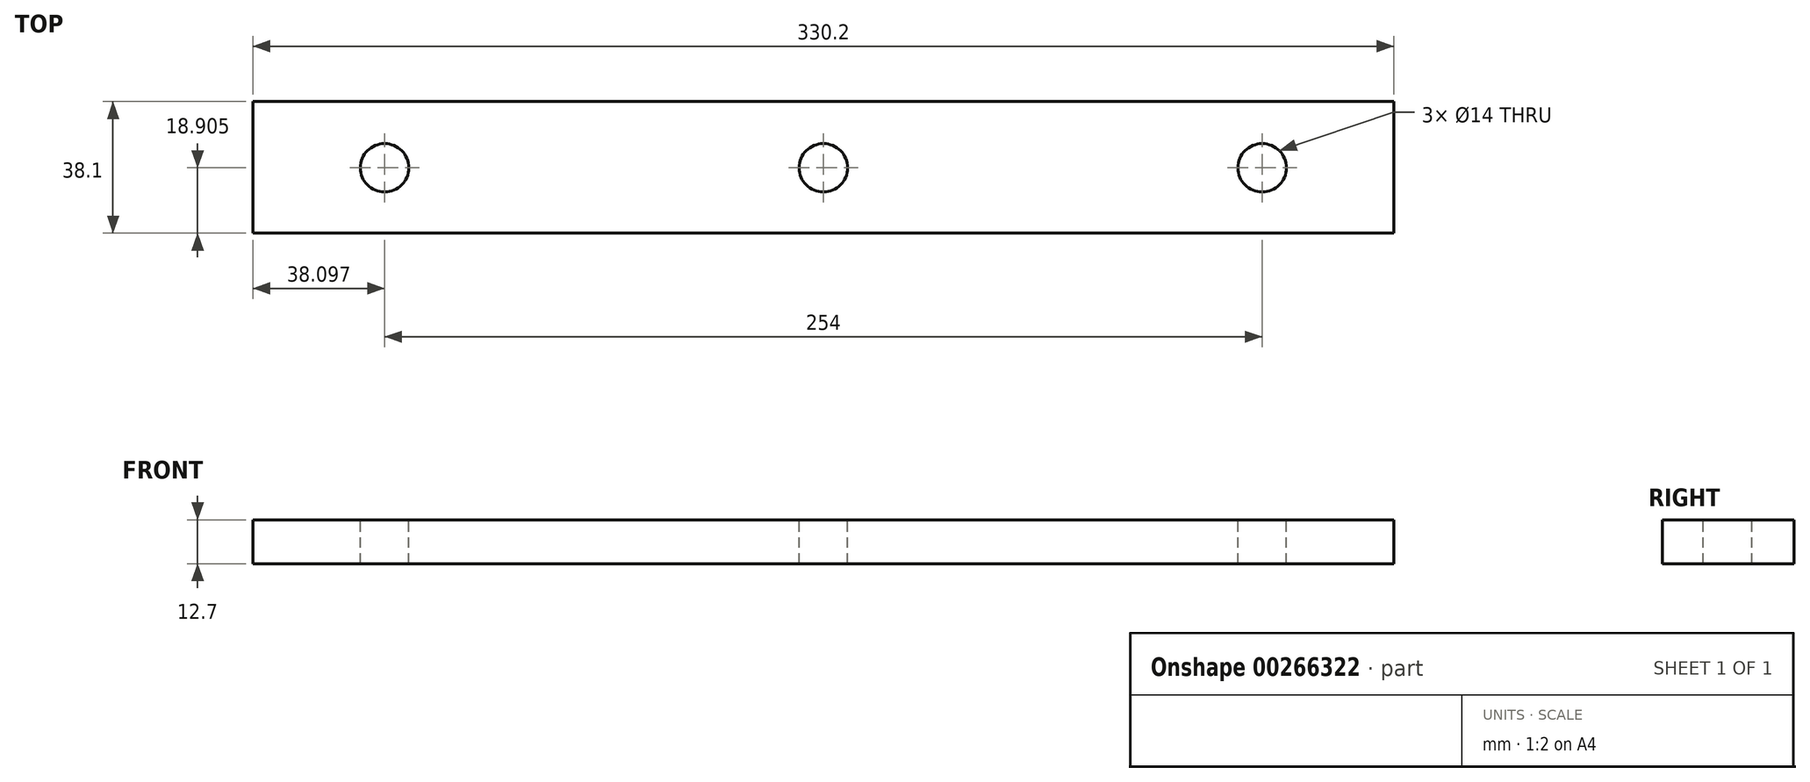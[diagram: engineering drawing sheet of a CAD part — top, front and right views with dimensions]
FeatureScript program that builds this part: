
annotation { "Feature Type Name" : "Feature", "Feature Type Description" : "" }
export const myFeature = defineFeature(function(context is Context, id is Id, definition is map)
    precondition{}
    {
        {
            var Q0;
            Q0=qCreatedBy(makeId("Top.planeOp"),FACE);
            var sketch = newSketch(context, id + "F0", { "sketchPlane" : qUnion([Q0])});
            skLineSegment(sketch, "E0.bottom", {"start": v(-30.27, -15.71) * mm, "end": v(299.93, -15.71) * mm});
            skLineSegment(sketch, "E0.top", {"start": v(-30.27, 22.39) * mm, "end": v(299.93, 22.39) * mm});
            skLineSegment(sketch, "E0.left", {"start": v(-30.27, -15.71) * mm, "end": v(-30.27, 22.39) * mm});
            skLineSegment(sketch, "E0.right", {"start": v(299.93, -15.71) * mm, "end": v(299.93, 22.39) * mm});
            skSolve(sketch);
        }
        {
            var Q0;
            Q0 = qSketchRegion(id + "F0", true);
            extrude(context, id + "F1", {"entities" : qUnion([Q0]), "depth" : 12.7 * mm});
        }
        {
            var Q0;
            Q0=makeQuery(id+"F1.opExtrude","CAP_FACE",FACE,{"disambiguationData":[OSD([sQuery(id+"F0.wireOp",EDGE,"E0.bottom"),sQuery(id+"F0.wireOp",EDGE,"E0.top"),sQuery(id+"F0.wireOp",EDGE,"E0.left"),sQuery(id+"F0.wireOp",EDGE,"E0.right")])],"isStart":false});
            var sketch = newSketch(context, id + "F2", { "sketchPlane" : qUnion([Q0])});
            skCircle(sketch, "E1", {"center": v(7.83, 3.2) * mm, "radius": 7 * mm});
            skCircle(sketch, "E2", {"center": v(261.83, 3.2) * mm, "radius": 7 * mm});
            skCircle(sketch, "E3", {"center": v(134.83, 3.2) * mm, "radius": 7 * mm});
            skPoint(sketch, "E3.centerSnap0", {"position": v(134.83, 22.39) * mm});
            skSolve(sketch);
        }
        {
            var Q0;
            Q0=makeQuery(id+"F2.imprint","IMPRINT",FACE,{"disambiguationData":[TD([[makeQuery(id+"F2.imprint","IMPRINT",EDGE,{"derivedFrom":sQuery(id+"F2.wireOp",EDGE,"E1")}),1.0]])]});
            var Q1;
            Q1=makeQuery(id+"F2.imprint","IMPRINT",FACE,{"disambiguationData":[TD([[makeQuery(id+"F2.imprint","IMPRINT",EDGE,{"derivedFrom":sQuery(id+"F2.wireOp",EDGE,"E3")}),1.0]])]});
            var Q2;
            Q2=makeQuery(id+"F2.imprint","IMPRINT",FACE,{"disambiguationData":[TD([[makeQuery(id+"F2.imprint","IMPRINT",EDGE,{"derivedFrom":sQuery(id+"F2.wireOp",EDGE,"E2")}),1.0]])]});
            extrude(context, id + "F3", {"entities" : qUnion([Q0, Q1, Q2]), "operationType" : NewBodyOperationType.REMOVE, "endBound" : BoundingType.THROUGH_ALL, "oppositeDirection" : true, "depth" : 25 * mm});
        }
    });
